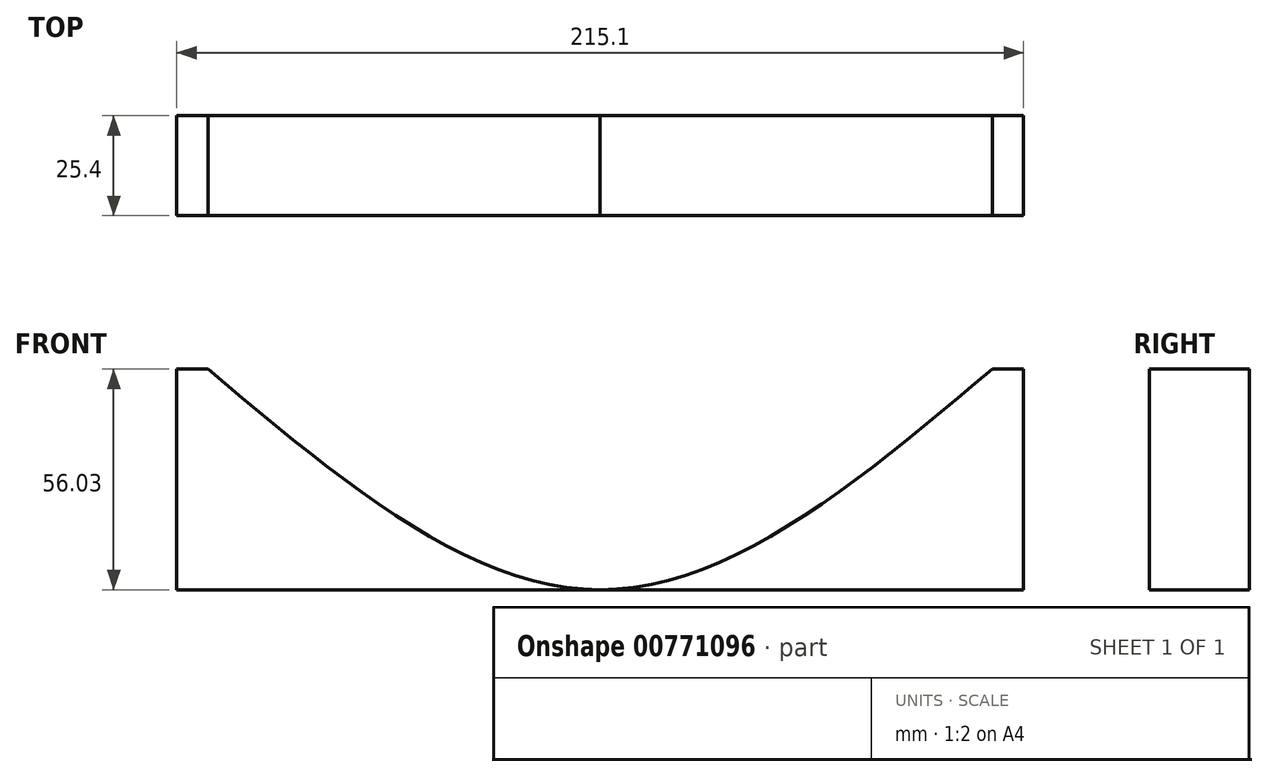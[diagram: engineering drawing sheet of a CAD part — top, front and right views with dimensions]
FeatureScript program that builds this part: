
annotation { "Feature Type Name" : "Feature", "Feature Type Description" : "" }
export const myFeature = defineFeature(function(context is Context, id is Id, definition is map)
    precondition{}
    {
        {
            var Q0;
            Q0=qCreatedBy(makeId("Front.planeOp"),FACE);
            var sketch = newSketch(context, id + "F0", { "sketchPlane" : qUnion([Q0])});
            skLineSegment(sketch, "E0", {"start": v(-99.6, 0) * mm, "end": v(-107.55, 0) * mm});
            skLineSegment(sketch, "E1", {"start": v(-107.55, 0) * mm, "end": v(-107.55, -75.49) * mm});
            skLineSegment(sketch, "E2", {"start": v(-107.55, -75.49) * mm, "end": v(-99.6, -75.49) * mm});
            skLineSegment(sketch, "E3", {"start": v(-99.6, -75.49) * mm, "end": v(-99.6, -2.6) * mm});
            skLineSegment(sketch, "E4", {"start": v(-99.6, -2.6) * mm, "end": v(-99.6, 0) * mm});
            skLineSegment(sketch, "E5", {"start": v(99.6, 0) * mm, "end": v(107.55, 0) * mm});
            skLineSegment(sketch, "E6", {"start": v(107.55, 0) * mm, "end": v(107.55, -75.49) * mm});
            skLineSegment(sketch, "E7", {"start": v(107.55, -75.49) * mm, "end": v(107.55, 0) * mm});
            skLineSegment(sketch, "E8", {"start": v(99.6, 0) * mm, "end": v(99.6, -75.49) * mm});
            skLineSegment(sketch, "E9", {"start": v(99.6, -75.49) * mm, "end": v(107.55, -75.49) * mm});
            skLineSegment(sketch, "E10", {"start": v(-99.6, -56.03) * mm, "end": v(99.6, -56.03) * mm});
            skFitSpline(sketch, "E11", {"points": [v(-99.6, 0) * mm, v(0, -56.03) * mm, v(99.6, 0) * mm], "startDerivative": vector(199.2, -168.1) * mm, "endDerivative": vector(199.2, 168.1) * mm});
            skLineSegment(sketch, "E12", {"start": v(-99.6, -56.03) * mm, "end": v(-163.71, -56.03) * mm});
            skLineSegment(sketch, "E13", {"start": v(99.6, -56.03) * mm, "end": v(161.8, -56.03) * mm});
            skFitSpline(sketch, "E14", {"points": [v(-107.55, 0) * mm, v(-163.71, -56.03) * mm], "startDerivative": vector(-56.17, -56.03) * mm, "endDerivative": vector(-56.17, -56.03) * mm});
            skFitSpline(sketch, "E15", {"points": [v(107.55, 0) * mm, v(161.8, -56.03) * mm], "startDerivative": vector(54.26, -56.03) * mm, "endDerivative": vector(54.26, -56.03) * mm});
            skSolve(sketch);
        }
        {
            var Q0;
            Q0=makeQuery(id+"F0.imprint","IMPRINT",FACE,{"disambiguationData":[TD([[makeQuery(id+"F0.imprint","IMPRINT",EDGE,{"derivedFrom":sQuery(id+"F0.wireOp",EDGE,"E0")}),1.0]])]});
            var Q1;
            {var subQ0=sQuery(id+"F0.wireOp",EDGE,"E4");Q1=makeQuery(id+"F0.imprint","IMPRINT",FACE,{"disambiguationData":[TD([[makeQuery(id+"F0.imprint","IMPRINT",EDGE,{"derivedFrom":subQ0}),-1.0]])]});}
            var Q2;
            {var subQ1=sQuery(id+"F0.wireOp",EDGE,"E8");var subQ3=sQuery(id+"F0.wireOp",EDGE,"E10");var subQ4=makeQuery(id+"F0.imprint","INTERSECT",VERTEX,{"derivedFrom":[subQ1,subQ3]});Q2=makeQuery(id+"F0.imprint","IMPRINT",FACE,{"disambiguationData":[TD([[makeQuery(id+"F0.imprint","IMPRINT",EDGE,{"disambiguationData":[TD([[subQ4,1.0]])],"derivedFrom":subQ3}),1.0]])]});}
            var Q3;
            {var subQ3=sQuery(id+"F0.wireOp",EDGE,"E5");Q3=makeQuery(id+"F0.imprint","IMPRINT",FACE,{"disambiguationData":[TD([[makeQuery(id+"F0.imprint","IMPRINT",EDGE,{"derivedFrom":subQ3}),-1.0]])]});}
            extrude(context, id + "F1", {"entities" : qUnion([Q0, Q1, Q2, Q3]), "depth" : 25.4 * mm, "offsetDistance" : 25.4 * mm});
        }
    });
